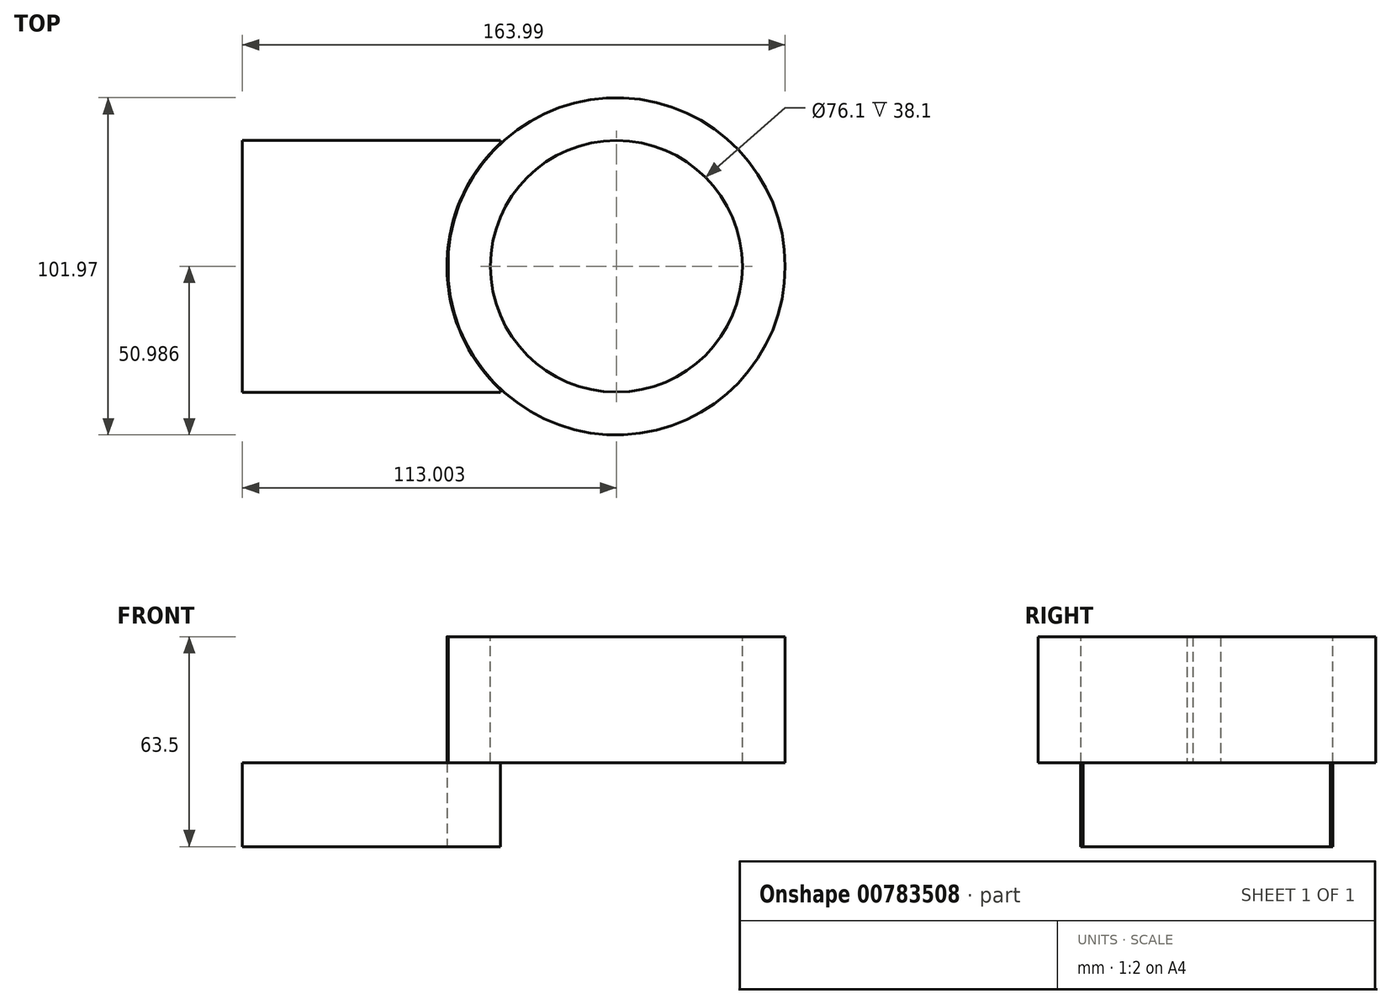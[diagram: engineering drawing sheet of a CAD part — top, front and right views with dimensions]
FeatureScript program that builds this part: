
annotation { "Feature Type Name" : "Feature", "Feature Type Description" : "" }
export const myFeature = defineFeature(function(context is Context, id is Id, definition is map)
    precondition{}
    {
        {
            var Q0;
            Q0=qCreatedBy(makeId("Top.planeOp"),FACE);
            var sketch = newSketch(context, id + "F0", { "sketchPlane" : qUnion([Q0])});
            skLineSegment(sketch, "E0.bottom", {"start": v(-60.88, -37.23) * mm, "end": v(17.08, -37.23) * mm});
            skLineSegment(sketch, "E0.top", {"start": v(-60.88, 38.98) * mm, "end": v(17.08, 38.98) * mm});
            skLineSegment(sketch, "E0.left", {"start": v(-60.88, -37.23) * mm, "end": v(-60.88, 38.98) * mm});
            skLineSegment(sketch, "E0.right", {"start": v(17.08, -37.23) * mm, "end": v(17.08, 38.98) * mm});
            skCircle(sketch, "E1", {"center": v(52.12, 0.88) * mm, "radius": 51.2 * mm});
            skPoint(sketch, "E1.centerSnap0", {"position": v(17.08, 0.88) * mm});
            skSolve(sketch);
        }
        {
            var Q0;
            {var subQ1=sQuery(id+"F0.wireOp",EDGE,"E0.bottom");Q0=makeQuery(id+"F0.imprint","IMPRINT",FACE,{"disambiguationData":[TD([[makeQuery(id+"F0.imprint","IMPRINT",EDGE,{"derivedFrom":subQ1}),1.0]])]});}
            var Q1;
            {var subQ0=sQuery(id+"F0.wireOp",EDGE,"E1");var subQ1=sQuery(id+"F0.wireOp",EDGE,"E0.right");var subQ2=makeQuery(id+"F0.imprint","INTERSECT",VERTEX,{"disambiguationData":[OD(0.0)],"derivedFrom":[subQ1,subQ0]});Q1=makeQuery(id+"F0.imprint","IMPRINT",FACE,{"disambiguationData":[TD([[makeQuery(id+"F0.imprint","IMPRINT",EDGE,{"disambiguationData":[TD([[subQ2,-1.0]])],"derivedFrom":subQ1}),-1.0]])]});}
            var Q2;
            {var subQ0=sQuery(id+"F0.wireOp",EDGE,"E1");var subQ1=sQuery(id+"F0.wireOp",EDGE,"E0.right");var subQ2=makeQuery(id+"F0.imprint","INTERSECT",VERTEX,{"disambiguationData":[OD(0.0)],"derivedFrom":[subQ1,subQ0]});Q2=makeQuery(id+"F0.imprint","IMPRINT",FACE,{"disambiguationData":[TD([[makeQuery(id+"F0.imprint","IMPRINT",EDGE,{"disambiguationData":[TD([[subQ2,-1.0]])],"derivedFrom":subQ1}),1.0]])]});}
            extrude(context, id + "F1", {"entities" : qUnion([Q0, Q1, Q2]), "depth" : 25.4 * mm, "offsetDistance" : 25.4 * mm});
        }
        {
            var Q0;
            Q0=makeQuery(id+"F1.opExtrude","CAP_FACE",FACE,{"disambiguationData":[OSD([sQuery(id+"F0.wireOp",EDGE,"E0.bottom"),sQuery(id+"F0.wireOp",EDGE,"E0.top"),sQuery(id+"F0.wireOp",EDGE,"E0.left"),sQuery(id+"F0.wireOp",EDGE,"E0.right"),sQuery(id+"F0.wireOp",EDGE,"E1")])],"isStart":false});
            var sketch = newSketch(context, id + "F2", { "sketchPlane" : qUnion([Q0])});
            skCircle(sketch, "E2", {"center": v(52.12, 0.88) * mm, "radius": 50.99 * mm});
            skSolve(sketch);
        }
        {
            var Q0;
            Q0=makeQuery(id+"F2.imprint","IMPRINT",FACE,{"disambiguationData":[TD([[makeQuery(id+"F2.imprint","IMPRINT",EDGE,{"derivedFrom":sQuery(id+"F2.wireOp",EDGE,"E2")}),1.0]])]});
            extrude(context, id + "F3", {"entities" : qUnion([Q0]), "operationType" : NewBodyOperationType.ADD, "depth" : 38.1 * mm, "offsetDistance" : 25.4 * mm});
        }
        {
            var Q0;
            Q0=makeQuery(id+"F1.opExtrude","CAP_FACE",FACE,{"disambiguationData":[OSD([sQuery(id+"F0.wireOp",EDGE,"E0.bottom"),sQuery(id+"F0.wireOp",EDGE,"E0.top"),sQuery(id+"F0.wireOp",EDGE,"E0.left"),sQuery(id+"F0.wireOp",EDGE,"E0.right"),sQuery(id+"F0.wireOp",EDGE,"E1")])],"isStart":false});
            var sketch = newSketch(context, id + "F4", { "sketchPlane" : qUnion([Q0])});
            skLineSegment(sketch, "E3", {"start": v(-60.88, 5.11) * mm, "end": v(1.31, 5.11) * mm});
            skLineSegment(sketch, "E4", {"start": v(-60.88, -5.11) * mm, "end": v(0, -5.11) * mm});
            skLineSegment(sketch, "E5", {"start": v(-60.88, 5.11) * mm, "end": v(-60.88, -5.11) * mm});
            skLineSegment(sketch, "E6", {"start": v(1.31, 5.11) * mm, "end": v(1.31, -5.11) * mm});
            skLineSegment(sketch, "E7", {"start": v(0, -5.11) * mm, "end": v(1.31, -5.11) * mm});
            skSolve(sketch);
        }
        {
            var Q0;
            {var subQ4=sQuery(id+"F4.wireOp",EDGE,"E3");Q0=makeQuery(id+"F4.imprint","IMPRINT",FACE,{"disambiguationData":[TD([[makeQuery(id+"F4.imprint","IMPRINT",EDGE,{"derivedFrom":subQ4}),-1.0]])]});}
            extrude(context, id + "F5", {"entities" : qUnion([Q0]), "operationType" : NewBodyOperationType.ADD, "depth" : 38.1 * mm, "offsetDistance" : 25.4 * mm});
        }
        {
            var Q0;
            Q0=makeQuery(id+"F5.opExtrude","SWEPT_FACE",FACE,{"disambiguationData":[OSD([sQuery(id+"F4.wireOp",EDGE,"E4"),sQuery(id+"F4.wireOp",EDGE,"E7")])]});
            var sketch = newSketch(context, id + "F6", { "sketchPlane" : qUnion([Q0])});
            skLineSegment(sketch, "E8", {"start": v(-60.88, 25.4) * mm, "end": v(1.31, 63.5) * mm});
            skSolve(sketch);
        }
        {
            var Q0;
            Q0=makeQuery(id+"F6.imprint","IMPRINT",FACE,{"disambiguationData":[TD([[makeQuery(id+"F6.imprint","IMPRINT",EDGE,{"derivedFrom":sQuery(id+"F6.wireOp",EDGE,"E8")}),1.0]])]});
            extrude(context, id + "F7", {"entities" : qUnion([Q0]), "operationType" : NewBodyOperationType.REMOVE, "oppositeDirection" : true, "depth" : 25.4 * mm, "offsetDistance" : 25.4 * mm});
        }
        {
            var Q0;
            {var subQ0=sQuery(id+"F2.wireOp",EDGE,"E2");Q0=makeQuery(id+"F5.boolean.opBoolean","MERGE",FACE,{"derivedFrom":[makeQuery(id+"F3.opExtrude","CAP_FACE",FACE,{"disambiguationData":[OSD([subQ0])],"isStart":false}),makeQuery(id+"F5.opExtrude","CAP_FACE",FACE,{"disambiguationData":[OSD([subQ0,sQuery(id+"F4.wireOp",EDGE,"E3"),sQuery(id+"F4.wireOp",EDGE,"E4"),sQuery(id+"F4.wireOp",EDGE,"E5"),sQuery(id+"F4.wireOp",EDGE,"E6"),sQuery(id+"F4.wireOp",EDGE,"E7")])],"isStart":false})]});}
            var sketch = newSketch(context, id + "F8", { "sketchPlane" : qUnion([Q0])});
            skCircle(sketch, "E9", {"center": v(52.12, 0.88) * mm, "radius": 38.05 * mm});
            skSolve(sketch);
        }
        {
            var Q0;
            Q0=makeQuery(id+"F8.imprint","IMPRINT",FACE,{"disambiguationData":[TD([[makeQuery(id+"F8.imprint","IMPRINT",EDGE,{"derivedFrom":sQuery(id+"F8.wireOp",EDGE,"E9")}),1.0]])]});
            extrude(context, id + "F9", {"entities" : qUnion([Q0]), "operationType" : NewBodyOperationType.REMOVE, "oppositeDirection" : true, "depth" : 63.5 * mm, "offsetDistance" : 25.4 * mm});
        }
    });
